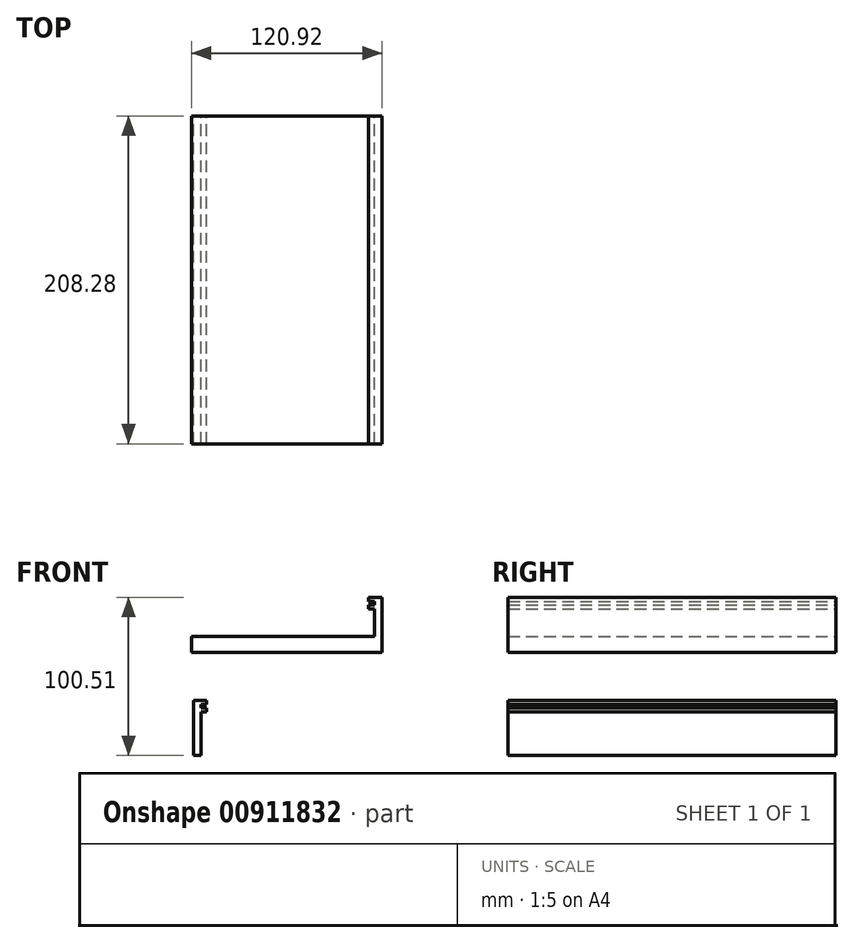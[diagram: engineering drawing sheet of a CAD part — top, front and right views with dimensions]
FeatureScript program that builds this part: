
annotation { "Feature Type Name" : "Feature", "Feature Type Description" : "" }
export const myFeature = defineFeature(function(context is Context, id is Id, definition is map)
    precondition{}
    {
        {
            var Q0;
            Q0=qCreatedBy(makeId("Front.planeOp"),FACE);
            var sketch = newSketch(context, id + "F0", { "sketchPlane" : qUnion([Q0])});
            skLineSegment(sketch, "E0", {"start": v(-117.75, -14.52) * mm, "end": v(0, -14.52) * mm});
            skLineSegment(sketch, "E1", {"start": v(-117.75, -4.36) * mm, "end": v(-1.63, -4.36) * mm});
            skLineSegment(sketch, "E2", {"start": v(-1.63, -4.36) * mm, "end": v(-1.63, 13.1) * mm});
            skLineSegment(sketch, "E3", {"start": v(-1.63, 13.1) * mm, "end": v(-5.47, 13.1) * mm});
            skLineSegment(sketch, "E4", {"start": v(-5.47, 13.1) * mm, "end": v(-5.47, 15.63) * mm});
            skLineSegment(sketch, "E5", {"start": v(-5.47, 15.63) * mm, "end": v(-1.63, 15.63) * mm});
            skLineSegment(sketch, "E6", {"start": v(-1.63, 15.63) * mm, "end": v(-1.63, 17.92) * mm});
            skLineSegment(sketch, "E7", {"start": v(-1.63, 17.92) * mm, "end": v(-5.47, 17.92) * mm});
            skLineSegment(sketch, "E8", {"start": v(-5.47, 17.92) * mm, "end": v(-5.47, 20.46) * mm});
            skLineSegment(sketch, "E9", {"start": v(0, 20.46) * mm, "end": v(0, -14.52) * mm});
            skLineSegment(sketch, "E10", {"start": v(-5.47, 20.46) * mm, "end": v(0, 20.46) * mm});
            skPoint(sketch, "E11", {"position": v(-59.7, -14.52) * mm});
            skPoint(sketch, "E12", {"position": v(-59.7, -4.36) * mm});
            skLineSegment(sketch, "E13", {"start": v(0, 20.46) * mm, "end": v(3.18, 20.46) * mm});
            skLineSegment(sketch, "E14", {"start": v(3.18, 20.46) * mm, "end": v(3.18, -14.52) * mm});
            skLineSegment(sketch, "E15", {"start": v(3.18, -14.52) * mm, "end": v(0, -14.52) * mm});
            skLineSegment(sketch, "E16", {"start": v(-113.24, -45.07) * mm, "end": v(-113.24, -80.05) * mm});
            skLineSegment(sketch, "E17", {"start": v(-113.24, -45.07) * mm, "end": v(-108.16, -45.07) * mm});
            skLineSegment(sketch, "E18", {"start": v(-108.16, -45.07) * mm, "end": v(-108.16, -47.6) * mm});
            skLineSegment(sketch, "E19", {"start": v(-108.16, -47.6) * mm, "end": v(-111.62, -47.6) * mm});
            skLineSegment(sketch, "E20", {"start": v(-111.62, -47.6) * mm, "end": v(-111.62, -49.9) * mm});
            skLineSegment(sketch, "E21", {"start": v(-111.62, -49.9) * mm, "end": v(-108.16, -49.9) * mm});
            skLineSegment(sketch, "E22", {"start": v(-108.16, -49.9) * mm, "end": v(-108.16, -52.43) * mm});
            skLineSegment(sketch, "E23", {"start": v(-108.16, -52.43) * mm, "end": v(-111.62, -52.43) * mm});
            skLineSegment(sketch, "E24", {"start": v(-111.62, -52.43) * mm, "end": v(-111.62, -69.89) * mm});
            skLineSegment(sketch, "E25", {"start": v(-113.24, -80.05) * mm, "end": v(-116.42, -80.05) * mm});
            skLineSegment(sketch, "E26", {"start": v(-116.42, -80.05) * mm, "end": v(-116.42, -45.07) * mm});
            skLineSegment(sketch, "E27", {"start": v(-116.42, -45.07) * mm, "end": v(-113.24, -45.07) * mm});
            skLineSegment(sketch, "E28", {"start": v(-117.75, -4.36) * mm, "end": v(-117.75, -14.52) * mm});
            skLineSegment(sketch, "E29", {"start": v(-111.62, -69.89) * mm, "end": v(-111.62, -80.05) * mm});
            skLineSegment(sketch, "E30", {"start": v(-111.62, -80.05) * mm, "end": v(-113.24, -80.05) * mm});
            skSolve(sketch);
        }
        {
            var Q0;
            Q0 = qSketchRegion(id + "F0", true);
            extrude(context, id + "F1", {"entities" : qUnion([Q0]), "depth" : 208.28 * mm, "offsetDistance" : 25.4 * mm});
        }
    });
